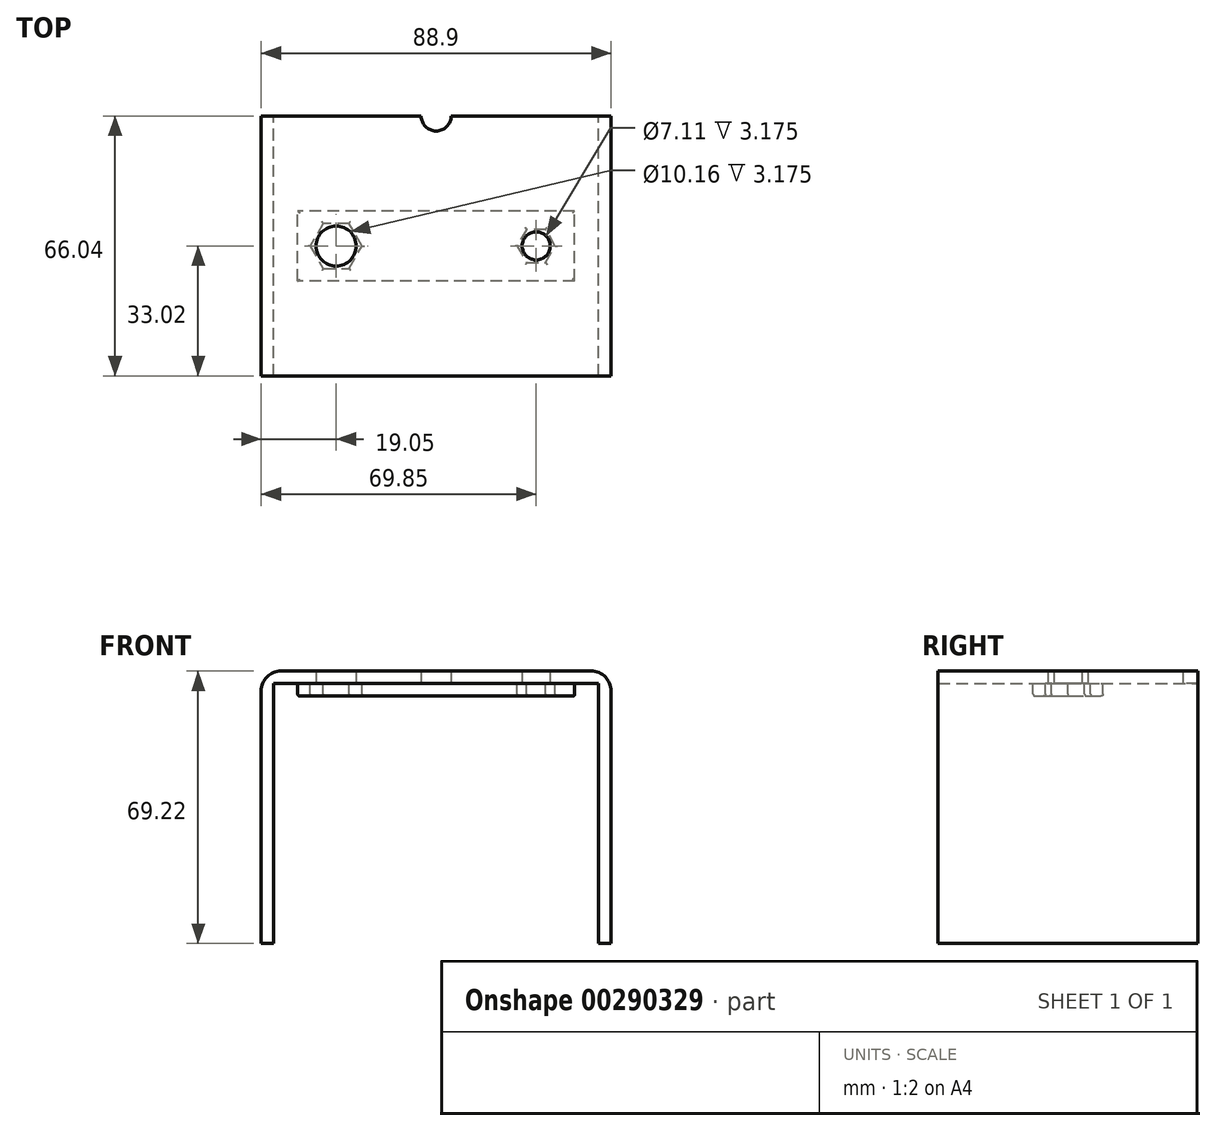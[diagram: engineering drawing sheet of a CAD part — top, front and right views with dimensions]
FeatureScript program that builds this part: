
annotation { "Feature Type Name" : "Feature", "Feature Type Description" : "" }
export const myFeature = defineFeature(function(context is Context, id is Id, definition is map)
    precondition{}
    {
        {
            var Q0;
            Q0=qCreatedBy(makeId("Top.planeOp"),FACE);
            var sketch = newSketch(context, id + "F0", { "sketchPlane" : qUnion([Q0])});
            skLineSegment(sketch, "E0.bottom", {"start": v(44.45, 33.02) * mm, "end": v(-44.45, 33.02) * mm});
            skLineSegment(sketch, "E0.top", {"start": v(44.45, -33.02) * mm, "end": v(-44.45, -33.02) * mm});
            skLineSegment(sketch, "E0.left", {"start": v(44.45, 33.02) * mm, "end": v(44.45, -33.02) * mm});
            skLineSegment(sketch, "E0.right", {"start": v(-44.45, 33.02) * mm, "end": v(-44.45, -33.02) * mm});
            skPoint(sketch, "E0.middle", {"position": v(0, 0) * mm});
            skLineSegment(sketch, "E1", {"start": v(-41.28, -33.02) * mm, "end": v(-41.28, 33.02) * mm});
            skLineSegment(sketch, "E2", {"start": v(41.28, -33.02) * mm, "end": v(41.28, 33.02) * mm});
            skArc(sketch, "E3", {"start": v(-3.81, 33.02) * mm, "mid": v(0, 29.21) * mm, "end": v(3.81, 33.02) * mm});
            skSolve(sketch);
        }
        {
            var Q0;
            {var subQ0=sQuery(id+"F0.wireOp",EDGE,"E0.left");Q0=makeQuery(id+"F0.imprint","IMPRINT",FACE,{"disambiguationData":[TD([[makeQuery(id+"F0.imprint","IMPRINT",EDGE,{"derivedFrom":subQ0}),-1.0]])]});}
            var Q1;
            {var subQ0=sQuery(id+"F0.wireOp",EDGE,"E0.right");Q1=makeQuery(id+"F0.imprint","IMPRINT",FACE,{"disambiguationData":[TD([[makeQuery(id+"F0.imprint","IMPRINT",EDGE,{"derivedFrom":subQ0}),1.0]])]});}
            var Q2;
            {var subQ0=sQuery(id+"F0.wireOp",EDGE,"E1");Q2=makeQuery(id+"F0.imprint","IMPRINT",FACE,{"disambiguationData":[TD([[makeQuery(id+"F0.imprint","IMPRINT",EDGE,{"derivedFrom":subQ0}),-1.0]])]});}
            extrude(context, id + "F1", {"entities" : qUnion([Q0, Q1, Q2]), "depth" : 3.17 * mm});
        }
        {
            var Q0;
            {var subQ0=sQuery(id+"F0.wireOp",EDGE,"E0.right");Q0=makeQuery(id+"F0.imprint","IMPRINT",FACE,{"disambiguationData":[TD([[makeQuery(id+"F0.imprint","IMPRINT",EDGE,{"derivedFrom":subQ0}),1.0]])]});}
            var Q1;
            {var subQ0=sQuery(id+"F0.wireOp",EDGE,"E0.left");Q1=makeQuery(id+"F0.imprint","IMPRINT",FACE,{"disambiguationData":[TD([[makeQuery(id+"F0.imprint","IMPRINT",EDGE,{"derivedFrom":subQ0}),-1.0]])]});}
            extrude(context, id + "F2", {"entities" : qUnion([Q0, Q1]), "operationType" : NewBodyOperationType.ADD, "oppositeDirection" : true, "depth" : 66.04 * mm});
        }
        {
            var Q0;
            Q0=makeQuery(id+"F1.opExtrude","CAP_EDGE",EDGE,{"disambiguationData":[OSD([sQuery(id+"F0.wireOp",EDGE,"E0.right")])],"isStart":false});
            var Q1;
            Q1=makeQuery(id+"F1.opExtrude","CAP_EDGE",EDGE,{"disambiguationData":[OSD([sQuery(id+"F0.wireOp",EDGE,"E0.left")])],"isStart":false});
            fillet(context, id + "F3", {"entities" : qUnion([Q0, Q1]), "radius" : 5.08 * mm, "tangentPropagation" : true, "allowEdgeOverflow" : false});
        }
        {
            var Q0;
            Q0=makeQuery(id+"F1.opExtrude","CAP_FACE",FACE,{"disambiguationData":[OSD([sQuery(id+"F0.wireOp",EDGE,"E0.bottom"),sQuery(id+"F0.wireOp",EDGE,"E0.top"),sQuery(id+"F0.wireOp",EDGE,"E0.left"),sQuery(id+"F0.wireOp",EDGE,"E0.right"),sQuery(id+"F0.wireOp",EDGE,"E3")])],"isStart":true});
            var sketch = newSketch(context, id + "F4", { "sketchPlane" : qUnion([Q0])});
            skLineSegment(sketch, "E4", {"start": v(-25.4, 0) * mm, "end": v(25.4, 0) * mm, "construction": true});
            skCircle(sketch, "E5.cCircle", {"center": v(25.4, 0) * mm, "radius": 4.2 * mm, "construction": true});
            skLineSegment(sketch, "E5.0", {"start": v(27.82, -4.2) * mm, "end": v(22.98, -4.2) * mm});
            skLineSegment(sketch, "E5.1", {"start": v(22.98, -4.2) * mm, "end": v(20.56, 0) * mm});
            skLineSegment(sketch, "E5.2", {"start": v(20.56, 0) * mm, "end": v(22.98, 4.2) * mm});
            skLineSegment(sketch, "E5.3", {"start": v(22.98, 4.2) * mm, "end": v(27.82, 4.2) * mm});
            skLineSegment(sketch, "E5.4", {"start": v(27.82, 4.2) * mm, "end": v(30.24, 0) * mm});
            skLineSegment(sketch, "E5.5", {"start": v(30.24, 0) * mm, "end": v(27.82, -4.2) * mm});
            skPoint(sketch, "E5.0.midPoint", {"position": v(25.4, -4.2) * mm});
            skCircle(sketch, "E6.cCircle", {"center": v(-25.4, 0) * mm, "radius": 5.71 * mm, "construction": true});
            skLineSegment(sketch, "E6.0", {"start": v(-22.1, -5.72) * mm, "end": v(-28.7, -5.71) * mm});
            skLineSegment(sketch, "E6.1", {"start": v(-28.7, -5.72) * mm, "end": v(-32, 0) * mm});
            skLineSegment(sketch, "E6.2", {"start": v(-32, 0) * mm, "end": v(-28.7, 5.72) * mm});
            skLineSegment(sketch, "E6.3", {"start": v(-28.7, 5.72) * mm, "end": v(-22.1, 5.71) * mm});
            skLineSegment(sketch, "E6.4", {"start": v(-22.1, 5.72) * mm, "end": v(-18.8, 0) * mm});
            skLineSegment(sketch, "E6.5", {"start": v(-18.8, 0) * mm, "end": v(-22.1, -5.72) * mm});
            skPoint(sketch, "E6.0.midPoint", {"position": v(-25.4, -5.72) * mm});
            skCircle(sketch, "E7", {"center": v(-25.4, 0) * mm, "radius": 5.08 * mm});
            skCircle(sketch, "E8", {"center": v(25.4, 0) * mm, "radius": 3.56 * mm});
            skLineSegment(sketch, "E9.bottom", {"start": v(35.17, 8.9) * mm, "end": v(-35.17, 8.9) * mm});
            skLineSegment(sketch, "E9.top", {"start": v(35.17, -8.9) * mm, "end": v(-35.17, -8.9) * mm});
            skLineSegment(sketch, "E9.left", {"start": v(35.17, 8.89) * mm, "end": v(35.17, -8.89) * mm});
            skLineSegment(sketch, "E9.right", {"start": v(-35.17, 8.89) * mm, "end": v(-35.17, -8.89) * mm});
            skPoint(sketch, "E9.middle", {"position": v(0, 0) * mm});
            skSolve(sketch);
        }
        {
            var Q0;
            Q0 = qSketchRegion(id + "F4", true);
            extrude(context, id + "F5", {"entities" : qUnion([Q0]), "operationType" : NewBodyOperationType.ADD, "depth" : 3.17 * mm});
        }
        {
            var Q0;
            Q0=makeQuery(id+"F4.imprint","IMPRINT",FACE,{"disambiguationData":[TD([[makeQuery(id+"F4.imprint","IMPRINT",EDGE,{"derivedFrom":sQuery(id+"F4.wireOp",EDGE,"E7")}),1.0]])]});
            var Q1;
            Q1=makeQuery(id+"F4.imprint","IMPRINT",FACE,{"disambiguationData":[TD([[makeQuery(id+"F4.imprint","IMPRINT",EDGE,{"derivedFrom":sQuery(id+"F4.wireOp",EDGE,"E8")}),1.0]])]});
            extrude(context, id + "F6", {"entities" : qUnion([Q0, Q1]), "operationType" : NewBodyOperationType.REMOVE, "oppositeDirection" : true, "depth" : 25.4 * mm});
        }
        {
            var Q0;
            Q0=makeQuery(id+"F5.opExtrude","CAP_FACE",FACE,{"disambiguationData":[OSD([sQuery(id+"F4.wireOp",EDGE,"E5.0"),sQuery(id+"F4.wireOp",EDGE,"E5.1"),sQuery(id+"F4.wireOp",EDGE,"E5.2"),sQuery(id+"F4.wireOp",EDGE,"E5.3"),sQuery(id+"F4.wireOp",EDGE,"E5.4"),sQuery(id+"F4.wireOp",EDGE,"E5.5"),sQuery(id+"F4.wireOp",EDGE,"E6.0"),sQuery(id+"F4.wireOp",EDGE,"E6.1"),sQuery(id+"F4.wireOp",EDGE,"E6.2"),sQuery(id+"F4.wireOp",EDGE,"E6.3"),sQuery(id+"F4.wireOp",EDGE,"E6.4"),sQuery(id+"F4.wireOp",EDGE,"E6.5"),sQuery(id+"F4.wireOp",EDGE,"E9.bottom"),sQuery(id+"F4.wireOp",EDGE,"E9.top"),sQuery(id+"F4.wireOp",EDGE,"E9.left"),sQuery(id+"F4.wireOp",EDGE,"E9.right")])],"isStart":false});
            fillet(context, id + "F7", {"entities" : qUnion([Q0]), "radius" : 0.5 * mm, "tangentPropagation" : true, "allowEdgeOverflow" : false});
        }
    });
